# Revit family: Plumbing Fixture-Grease_Interseptor_Mifab_MI-E-O-HU
name_source: partatom
category: Plumbing Fixtures
revit_build: Autodesk Revit Structure 2013 (Build: 20120221_2030(x64)
units: mm (PartAtom-declared; Revit-internal decimal feet)

## types (17) — shared parameters
Assembly Code = D2090300
Description = Electronic Oil Interceptors With Integral Oil Storage Tank
Interceptor Material = Acid Resistant Epoxy Coated Green
Manufacturer = MIFAB
URL = www.mifab.com
zero-valued in all types: Default Elevation, WFU

## per-type parameters (varying)
| type | A | B | C | D | E | F | Flow Rate | G | Grease Capacity | Standard Inlet And Outlet Radii | Water Capacity |
| MI-E-O-HU-A | 24 " | 26 " | 4 " | 9 " | 13 " | 2 " | 10 GPM | 4 " | 74.93 lbs | 1 " | 10.66 Gallons |
| MI-E-O-HU-B | 26 " | 26.5 " | 4 " | 11 " | 15 " | 2 " | 15 GPM | 6 " | 102.40lbs | 1 " | 15.06 Gallons |
| MI-E-O-HU-C | 26 " | 26.5 " | 4 " | 13.5 " | 17.5 " | 3 " | 20 GPM | 8 " | 119.88 lbs | 1.5 " | 18.08 Gallons |
| MI-E-O-HU-1 | 29 " | 46 " | 4.5 " | 25.5 " | 30 " | 3 " | 25 GPM | 20 " | 542.60 lbs | 1.5 " | 63.12 Gallons |
| MI-E-O-HU-2 | 37 " | 44.5 " | 5 " | 26 " | 31 " | 3 " | 35 GPM | 20.5 " | 509.51 lbs | 1.5 " | 100.23 Gallons |
| MI-E-O-HU-3 | 43 " | 65.5 " | 6 " | 26 " | 32 " | 3 " | 50 GPM | 20.5 " | 977.19 lbs | 1.5 " | 163.07 Gallons |
| MI-E-O-HU-4 | 49 " | 65 " | 9.5 " | 26.5 " | 36 " | 4 " | 75 GPM | 20.5 " | 1015.90 lbs | 2 " | 201.89 Gallons |
| MI-E-O-HU-5 | 58 " | 90 " | 9.5 " | 26.5 " | 36 " | 4 " | 100 GPM | 20.5 " | 1984.34 lbs | 2 " | 302.91 Gallons |
| MI-E-O-HU-6 | 62 " | 90 " | 12 " | 28 " | 40 " | 4 " | 125 GPM | 22 " | 2245.97 lbs | 2 " | 344.42Gallons |
| MI-E-O-HU-7 | 66 " | 76 " | 14 " | 30 " | 44 " | 4 " | 150 GPM | 24 " | 1942.51 lbs | 2 " | 356.85 Gallons |
| MI-E-O-HU-8 | 73.25 " | 90 " | 17 " | 30.5 " | 48 " | 4 " | 200 GPM | 24.5 " | 2896.59 lbs | 2 " | 452.72 Gallons |
| MI-E-O-HU-9 | 73.25 " | 90 " | 15.5 " | 35.5 " | 51 " | 4 " | 250 GPM | 29.5 " | 2912.83 lbs | 2 " | 588.97 Gallons |
| MI-E-O-HU-10 | 94.875 " | 86 " | 15.5 " | 36.5 " | 52 " | 6 " | 300 GPM | 29.5 " | 2882.23 lbs | 3 " | 814.82 Gallons |
| MI-E-O-HU-11 | 100.875 " | 94 " | 16.5 " | 43.5 " | 60 " | 6 " | 350 GPM | 36.5 " | 4746.06 lbs | 3 " | 1066.06 Gallons |
| MI-E-O-HU-12 | 107.875 " | 91 " | 17 " | 43 " | 60 " | 6 " | 400 GPM | 36 " | 4693.61 lbs | 3 " | 1109.11 Gallons |
| MI-E-O-HU-13 | 118.875 " | 83 " | 17 " | 43 " | 60 " | 6 " | 450 GPM | 36 " | 4726.71 lbs | 3 " | 1113.05 Gallons |
| MI-E-O-HU-14 | 118.875 " | 83 " | 20 " | 46 " | 66 " | 6 " | 500 GPM | 39 " | 4667.39 lbs | 3 " | 1240.03 Gallons |

note: column(s) folded — value = type name in every type: Model

## geometry (parser evidence)
native form markers: Blend x7, Sweep x1
no freeform markers — native parametric forms only
